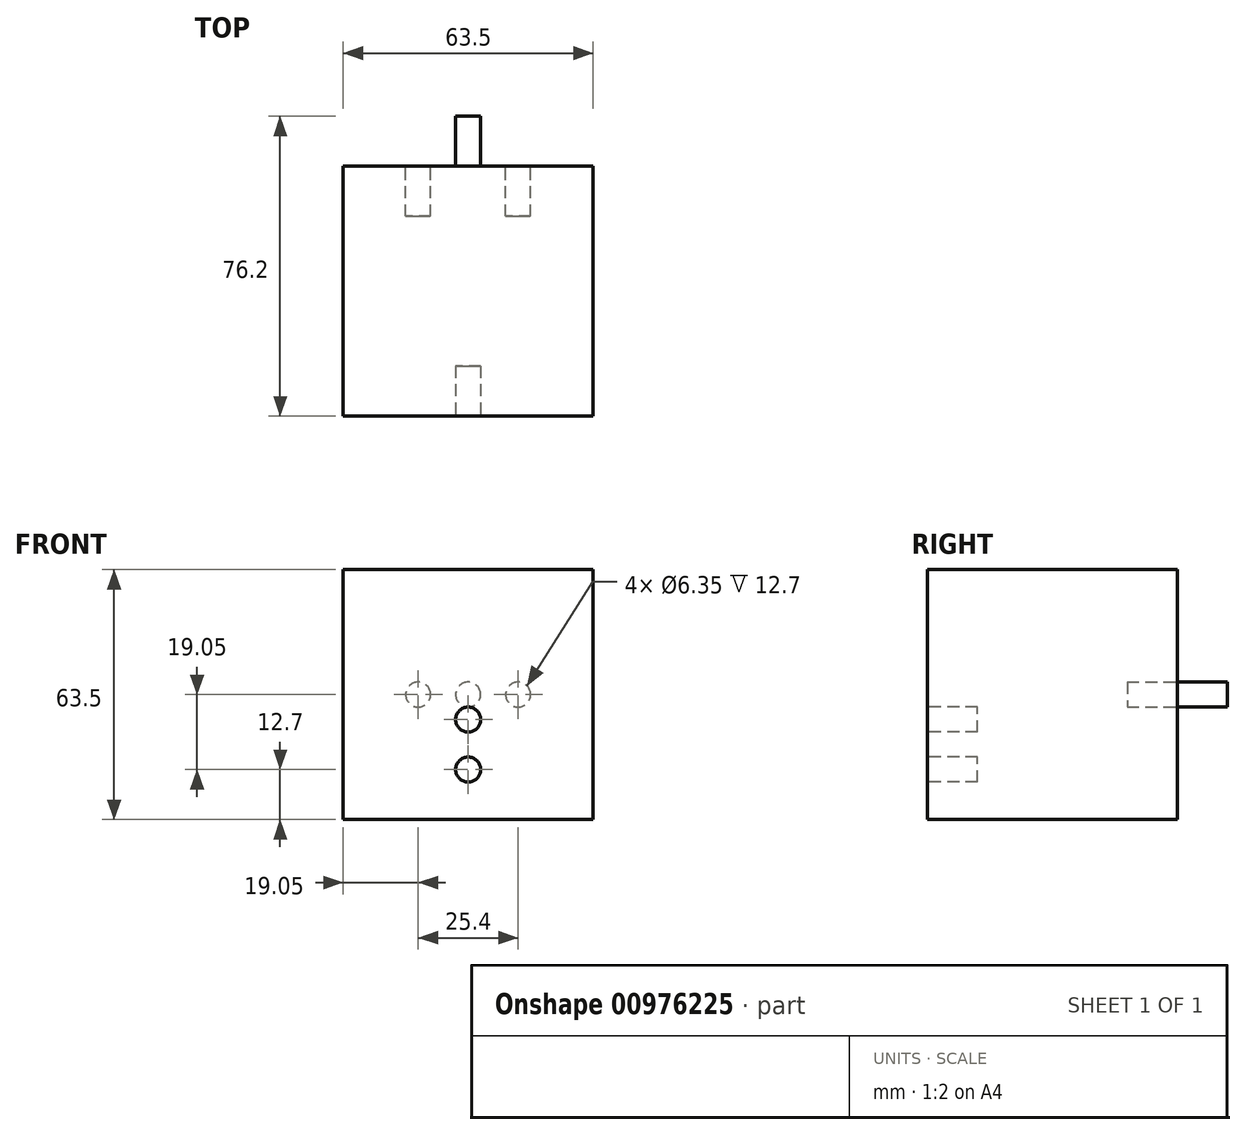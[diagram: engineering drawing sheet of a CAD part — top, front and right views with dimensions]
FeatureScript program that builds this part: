
annotation { "Feature Type Name" : "Feature", "Feature Type Description" : "" }
export const myFeature = defineFeature(function(context is Context, id is Id, definition is map)
    precondition{}
    {
        {
            var Q0;
            Q0=qCreatedBy(makeId("Top.planeOp"),FACE);
            var sketch = newSketch(context, id + "F0", { "sketchPlane" : qUnion([Q0])});
            skLineSegment(sketch, "E0.bottom", {"start": v(-31.75, 31.75) * mm, "end": v(31.75, 31.75) * mm});
            skLineSegment(sketch, "E0.top", {"start": v(-31.75, -31.75) * mm, "end": v(31.75, -31.75) * mm});
            skLineSegment(sketch, "E0.left", {"start": v(-31.75, 31.75) * mm, "end": v(-31.75, -31.75) * mm});
            skLineSegment(sketch, "E0.right", {"start": v(31.75, 31.75) * mm, "end": v(31.75, -31.75) * mm});
            skPoint(sketch, "E0.middle", {"position": v(0, 0) * mm});
            skSolve(sketch);
        }
        {
            var Q0;
            Q0=makeQuery(id+"F0.imprint","IMPRINT",FACE,{"disambiguationData":[TD([[makeQuery(id+"F0.imprint","IMPRINT",EDGE,{"derivedFrom":sQuery(id+"F0.wireOp",EDGE,"E0.bottom")}),-1.0]])]});
            extrude(context, id + "F1", {"entities" : qUnion([Q0]), "depth" : 63.5 * mm, "offsetDistance" : 25.4 * mm});
        }
        {
            var Q0;
            Q0=makeQuery(id+"F1.opExtrude","SWEPT_FACE",FACE,{"disambiguationData":[OSD([sQuery(id+"F0.wireOp",EDGE,"E0.bottom")])]});
            var sketch = newSketch(context, id + "F2", { "sketchPlane" : qUnion([Q0])});
            skCircle(sketch, "E1", {"center": v(0, 31.75) * mm, "radius": 3.18 * mm});
            skCircle(sketch, "E2", {"center": v(-12.7, 31.75) * mm, "radius": 3.18 * mm});
            skCircle(sketch, "E3", {"center": v(12.7, 31.75) * mm, "radius": 3.18 * mm});
            skSolve(sketch);
        }
        {
            var Q0;
            Q0=makeQuery(id+"F2.imprint","IMPRINT",FACE,{"disambiguationData":[TD([[makeQuery(id+"F2.imprint","IMPRINT",EDGE,{"derivedFrom":sQuery(id+"F2.wireOp",EDGE,"E1")}),1.0]])]});
            extrude(context, id + "F3", {"entities" : qUnion([Q0]), "operationType" : NewBodyOperationType.ADD, "depth" : 12.7 * mm, "offsetDistance" : 25.4 * mm});
        }
        {
            var Q0;
            Q0=makeQuery(id+"F2.imprint","IMPRINT",FACE,{"disambiguationData":[TD([[makeQuery(id+"F2.imprint","IMPRINT",EDGE,{"derivedFrom":sQuery(id+"F2.wireOp",EDGE,"E2")}),1.0]])]});
            var Q1;
            Q1=makeQuery(id+"F2.imprint","IMPRINT",FACE,{"disambiguationData":[TD([[makeQuery(id+"F2.imprint","IMPRINT",EDGE,{"derivedFrom":sQuery(id+"F2.wireOp",EDGE,"E3")}),1.0]])]});
            extrude(context, id + "F4", {"entities" : qUnion([Q0, Q1]), "operationType" : NewBodyOperationType.REMOVE, "oppositeDirection" : true, "depth" : 12.7 * mm, "offsetDistance" : 25.4 * mm});
        }
        {
            var Q0;
            Q0=makeQuery(id+"F1.opExtrude","SWEPT_FACE",FACE,{"disambiguationData":[OSD([sQuery(id+"F0.wireOp",EDGE,"E0.top")])]});
            var sketch = newSketch(context, id + "F5", { "sketchPlane" : qUnion([Q0])});
            skCircle(sketch, "E4", {"center": v(0, 25.4) * mm, "radius": 3.18 * mm});
            skCircle(sketch, "E5", {"center": v(0, 12.7) * mm, "radius": 3.17 * mm});
            skSolve(sketch);
        }
        {
            var Q0;
            Q0=makeQuery(id+"F5.imprint","IMPRINT",FACE,{"disambiguationData":[TD([[makeQuery(id+"F5.imprint","IMPRINT",EDGE,{"derivedFrom":sQuery(id+"F5.wireOp",EDGE,"E4")}),1.0]])]});
            var Q1;
            Q1=makeQuery(id+"F5.imprint","IMPRINT",FACE,{"disambiguationData":[TD([[makeQuery(id+"F5.imprint","IMPRINT",EDGE,{"derivedFrom":sQuery(id+"F5.wireOp",EDGE,"E5")}),1.0]])]});
            extrude(context, id + "F6", {"entities" : qUnion([Q0, Q1]), "operationType" : NewBodyOperationType.REMOVE, "oppositeDirection" : true, "depth" : 12.7 * mm, "offsetDistance" : 25.4 * mm});
        }
    });
